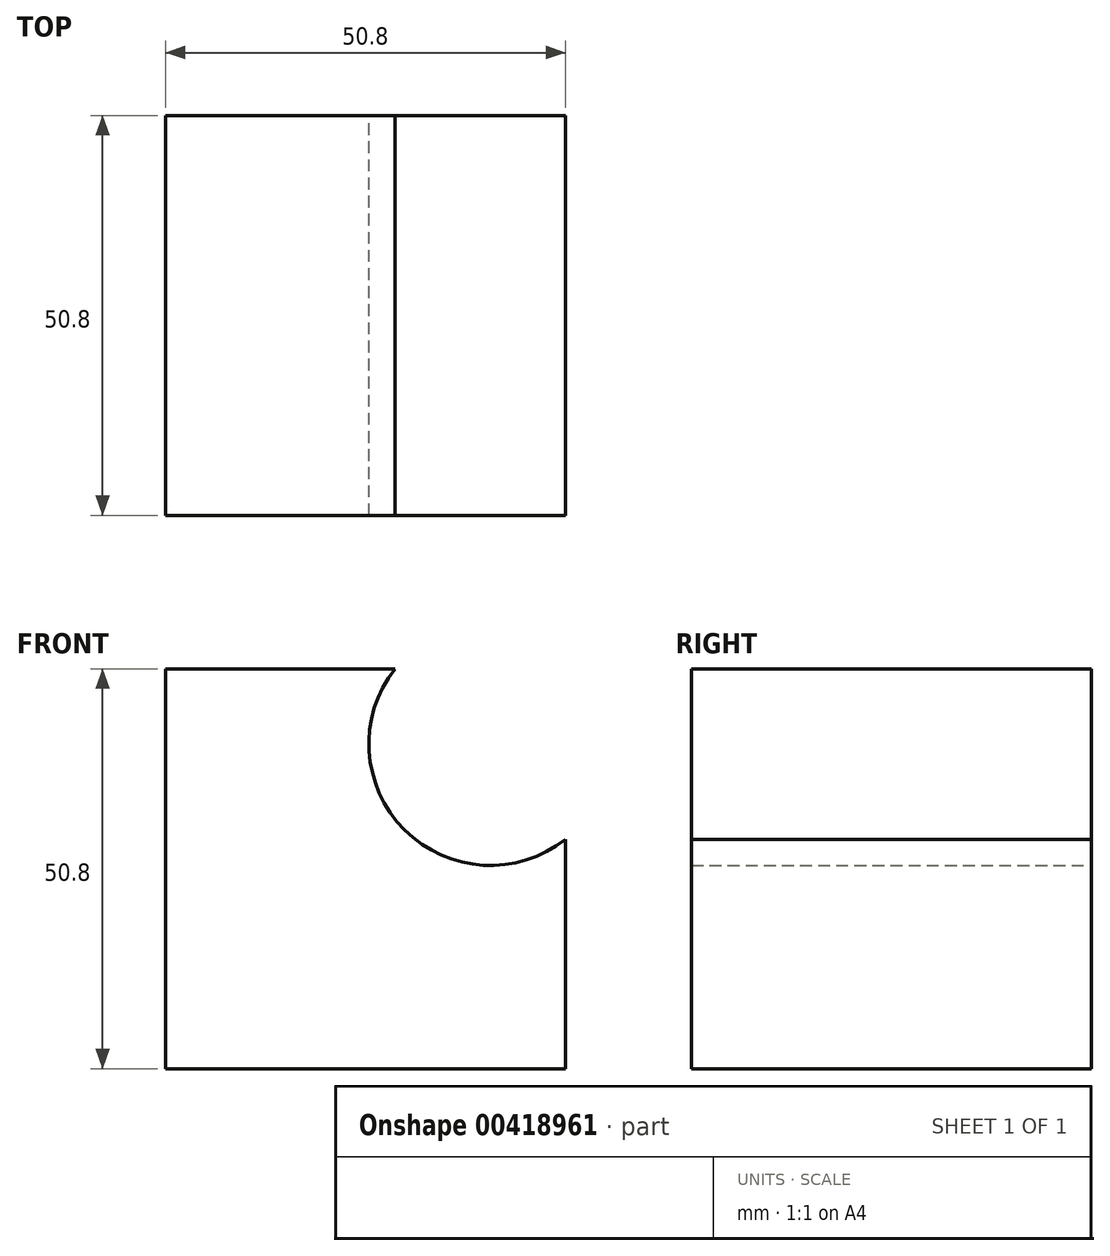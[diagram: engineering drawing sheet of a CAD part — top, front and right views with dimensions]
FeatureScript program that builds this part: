
annotation { "Feature Type Name" : "Feature", "Feature Type Description" : "" }
export const myFeature = defineFeature(function(context is Context, id is Id, definition is map)
    precondition{}
    {
        {
            var Q0;
            Q0=qCreatedBy(makeId("Front.planeOp"),FACE);
            var sketch = newSketch(context, id + "F0", { "sketchPlane" : qUnion([Q0])});
            skLineSegment(sketch, "E0.bottom", {"start": v(0, 0) * mm, "end": v(-50.8, 0) * mm});
            skLineSegment(sketch, "E0.top", {"start": v(0, 50.8) * mm, "end": v(-50.8, 50.8) * mm});
            skLineSegment(sketch, "E0.left", {"start": v(0, 0) * mm, "end": v(0, 50.8) * mm});
            skLineSegment(sketch, "E0.right", {"start": v(-50.8, 0) * mm, "end": v(-50.8, 50.8) * mm});
            skSolve(sketch);
        }
        {
            var Q0;
            Q0 = qSketchRegion(id + "F0", true);
            extrude(context, id + "F1", {"entities" : qUnion([Q0]), "depth" : 50.8 * mm});
        }
        {
            var Q0;
            Q0=qCreatedBy(makeId("Front.planeOp"),FACE);
            var sketch = newSketch(context, id + "F2", { "sketchPlane" : qUnion([Q0])});
            skCircle(sketch, "E1", {"center": v(-9.55, 41.25) * mm, "radius": 15.42 * mm});
            skSolve(sketch);
        }
        {
            var Q0;
            Q0 = qSketchRegion(id + "F2", true);
            extrude(context, id + "F3", {"entities" : qUnion([Q0]), "operationType" : NewBodyOperationType.REMOVE, "depth" : 51.56 * mm});
        }
    });
